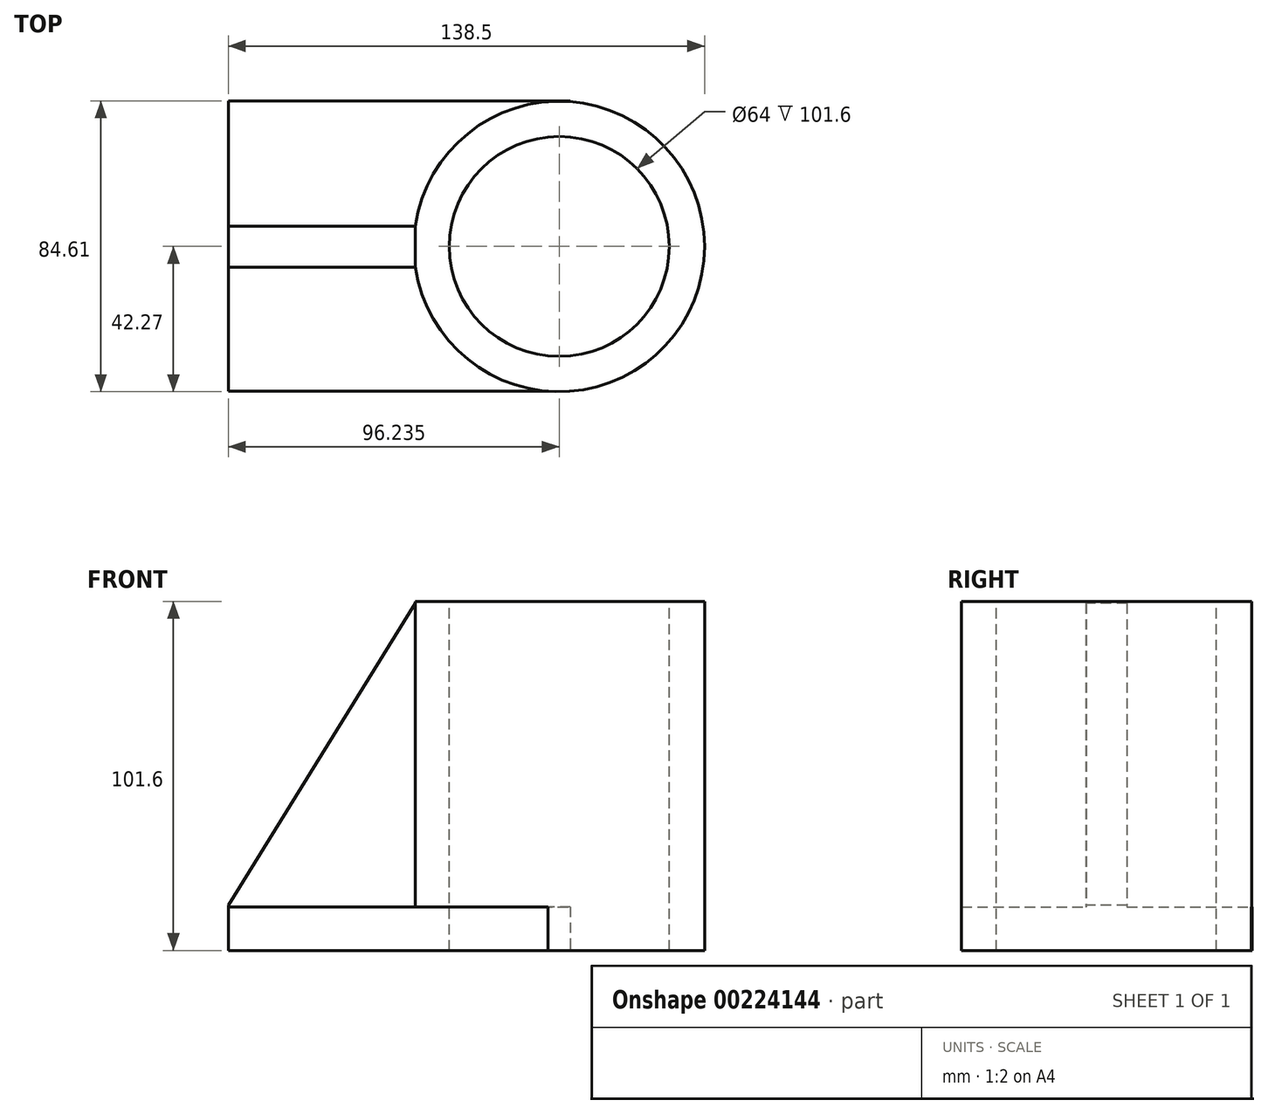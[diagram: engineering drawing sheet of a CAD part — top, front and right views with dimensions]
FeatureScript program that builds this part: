
annotation { "Feature Type Name" : "Feature", "Feature Type Description" : "" }
export const myFeature = defineFeature(function(context is Context, id is Id, definition is map)
    precondition{}
    {
        {
            var Q0;
            Q0=qCreatedBy(makeId("Top.planeOp"),FACE);
            var sketch = newSketch(context, id + "F0", { "sketchPlane" : qUnion([Q0])});
            skCircle(sketch, "E0", {"center": v(62.47, 0) * mm, "radius": 42.27 * mm});
            skSolve(sketch);
        }
        {
            var Q0;
            Q0 = qSketchRegion(id + "F0", true);
            extrude(context, id + "F1", {"entities" : qUnion([Q0]), "depth" : 101.6 * mm});
        }
        {
            var Q0;
            Q0=makeQuery(id+"F1.opExtrude","CAP_FACE",FACE,{"disambiguationData":[OSD([sQuery(id+"F0.wireOp",EDGE,"E0")])],"isStart":true});
            var sketch = newSketch(context, id + "F2", { "sketchPlane" : qUnion([Q0])});
            skLineSegment(sketch, "E1.bottom", {"start": v(65.73, 42.14) * mm, "end": v(-33.76, 42.14) * mm});
            skLineSegment(sketch, "E1.top", {"start": v(65.73, -42.34) * mm, "end": v(-33.76, -42.34) * mm});
            skLineSegment(sketch, "E1.left", {"start": v(65.73, 42.14) * mm, "end": v(65.73, -42.34) * mm});
            skLineSegment(sketch, "E1.right", {"start": v(-33.76, 42.14) * mm, "end": v(-33.76, -42.34) * mm});
            skSolve(sketch);
        }
        {
            var Q0;
            Q0 = qSketchRegion(id + "F2", true);
            extrude(context, id + "F3", {"entities" : qUnion([Q0]), "operationType" : NewBodyOperationType.ADD, "oppositeDirection" : true, "depth" : 12.7 * mm});
        }
        {
            var Q0;
            Q0=makeQuery(id+"F1.opExtrude","CAP_FACE",FACE,{"disambiguationData":[OSD([sQuery(id+"F0.wireOp",EDGE,"E0")])],"isStart":false});
            var sketch = newSketch(context, id + "F4", { "sketchPlane" : qUnion([Q0])});
            skCircle(sketch, "E2", {"center": v(62.47, 0) * mm, "radius": 32 * mm});
            skSolve(sketch);
        }
        {
            var Q0;
            Q0 = qSketchRegion(id + "F4", true);
            extrude(context, id + "F5", {"entities" : qUnion([Q0]), "operationType" : NewBodyOperationType.REMOVE, "endBound" : BoundingType.THROUGH_ALL, "oppositeDirection" : true, "depth" : 25.4 * mm});
        }
        {
            var Q0;
            Q0=makeQuery(id+"F3.opExtrude","CAP_FACE",FACE,{"disambiguationData":[OSD([sQuery(id+"F2.wireOp",EDGE,"E1.bottom"),sQuery(id+"F2.wireOp",EDGE,"E1.top"),sQuery(id+"F2.wireOp",EDGE,"E1.left"),sQuery(id+"F2.wireOp",EDGE,"E1.right")])],"isStart":false});
            var sketch = newSketch(context, id + "F6", { "sketchPlane" : qUnion([Q0])});
            skLineSegment(sketch, "E3.bottom", {"start": v(20.63, 5.94) * mm, "end": v(-33.76, 5.94) * mm});
            skLineSegment(sketch, "E3.top", {"start": v(20.63, -6.04) * mm, "end": v(-33.76, -6.04) * mm});
            skLineSegment(sketch, "E3.left", {"start": v(20.63, 5.94) * mm, "end": v(20.63, -6.04) * mm});
            skLineSegment(sketch, "E3.right", {"start": v(-33.76, 5.94) * mm, "end": v(-33.76, -6.04) * mm});
            skSolve(sketch);
        }
        {
            var Q0;
            Q0 = qSketchRegion(id + "F6", true);
            extrude(context, id + "F7", {"entities" : qUnion([Q0]), "operationType" : NewBodyOperationType.ADD, "depth" : 101.6 * mm});
        }
        {
            var Q0;
            Q0=makeQuery(id+"F7.opExtrude","SWEPT_FACE",FACE,{"disambiguationData":[OSD([sQuery(id+"F6.wireOp",EDGE,"E3.top")])]});
            var sketch = newSketch(context, id + "F8", { "sketchPlane" : qUnion([Q0])});
            skLineSegment(sketch, "E4", {"start": v(23.37, 105.4) * mm, "end": v(-35.56, 10.3) * mm});
            skLineSegment(sketch, "E5", {"start": v(-35.56, 10.3) * mm, "end": v(-58.31, 117.15) * mm});
            skLineSegment(sketch, "E6", {"start": v(-58.31, 117.15) * mm, "end": v(24.57, 117.15) * mm});
            skLineSegment(sketch, "E7", {"start": v(24.57, 116.9) * mm, "end": v(23.37, 105.4) * mm});
            skSolve(sketch);
        }
        {
            var Q0;
            Q0 = qSketchRegion(id + "F8", true);
            var Q1;
            {var subQ1=sQuery(id+"F6.wireOp",EDGE,"E3.top");var subQ6=makeQuery(id+"F7.opExtrude","CAP_EDGE",EDGE,{"disambiguationData":[OSD([subQ1])],"isStart":false});Q1=makeQuery(id+"F8.imprint","IMPRINT",FACE,{"disambiguationData":[TD([[makeQuery(id+"F8.imprint","IMPRINT",EDGE,{"derivedFrom":subQ6}),1.0]])]});}
            extrude(context, id + "F9", {"entities" : qUnion([Q0, Q1]), "operationType" : NewBodyOperationType.REMOVE, "endBound" : BoundingType.THROUGH_ALL, "oppositeDirection" : true, "depth" : 25.4 * mm});
        }
    });
